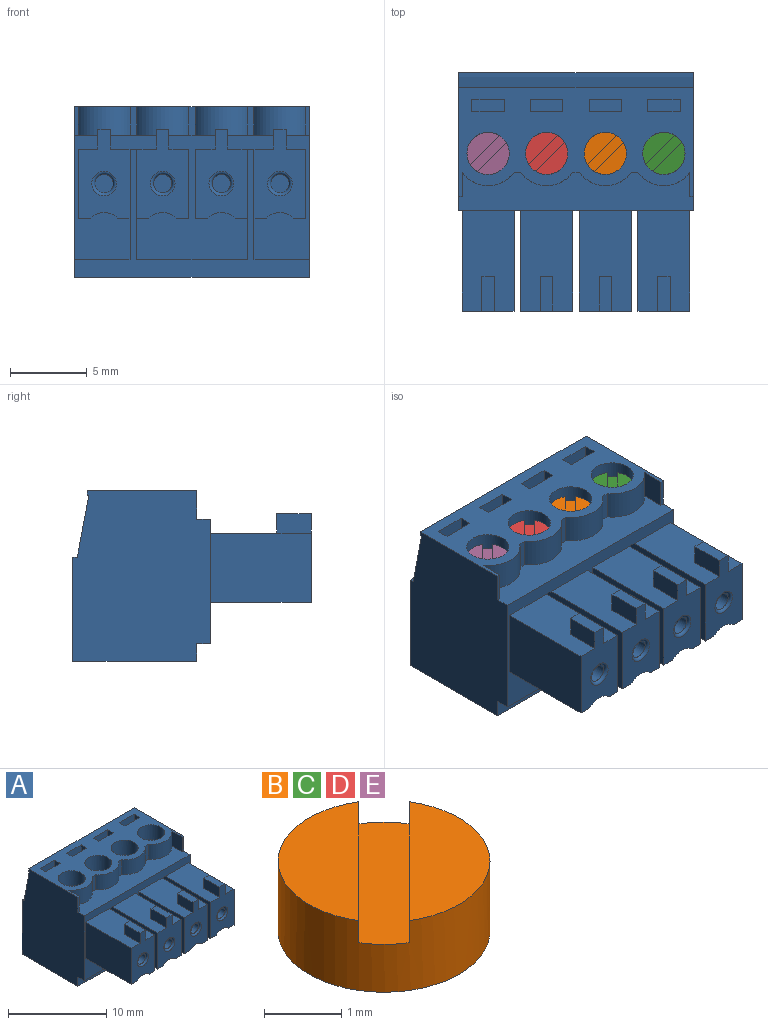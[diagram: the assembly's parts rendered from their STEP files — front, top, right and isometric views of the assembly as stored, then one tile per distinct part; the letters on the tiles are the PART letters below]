
ASSEMBLY  parts=5 mates=1
PART A: 140 faces, bbox 15.2x15.5x11.1 mm
  f0: plane 15.24x7.1mm, normal (0,0,1), area 62.7mm2, adj f5,f11,f12,f28,f29,f31,f39,f59
  f1: plane 15.24x8.34mm, normal (0,-1,0), area 24mm2, adj f3,f4,f5,f6,f16,f52,f58,f75
  f2: plane 15.24x8.08mm, normal (0,-1,0), area 58.1mm2, adj f3,f4,f5,f13,f14,f15,f16,f22
  f3: plane 0.9x0.44mm, normal (0,0,-1), area 0.4mm2, adj f1,f2,f16,f58
  f4: plane 3.59x0.9mm, normal (0,0,-1), area 3.2mm2, adj f1,f2,f5,f16
  f5: plane 11.1x8.95mm, normal (1,0,0), area 93.6mm2, adj f0,f1,f2,f4,f6,f7,f8,f9
  f6: plane 15.24x8.05mm, normal (0,0,-1), area 122.7mm2, adj f1,f5,f7,f77
  f7: plane 15.24x6.78mm, normal (0,1,0), area 55.1mm2, adj f5,f6,f8,f32,f33,f34,f35,f60
  f8: plane 15.24x0.3mm, normal (0,0,1), area 4.5mm2, adj f5,f7,f9,f77
  f9: plane 15.24x4.02mm, normal (0,0.98,0.18), area 62.3mm2, adj f5,f8,f10,f77
  f10: plane 15.24x0.1mm, normal (0,0,-1), area 1.4mm2, adj f5,f9,f11,f77
  f11: plane 15.24x0.3mm, normal (0,1,0), area 4.6mm2, adj f0,f5,f10,f77
  f12: plane 1.86x0.22mm, normal (0,-1,0), area 0.4mm2, adj f0,f5,f13,f28
  f13: plane 15.24x2.46mm, normal (0,0,1), area 28.7mm2, adj f2,f5,f12,f28,f29,f39,f64,f77
  f14: plane 6.55x3.37mm, normal (0,0,1), area 20.3mm2, adj f2,f15,f16,f17,f18,f19,f21
  f15: plane 6.55x4.49mm, normal (1,0,0), area 29.4mm2, adj f2,f14,f17,f22
  f16: plane 7.45x7.18mm, normal (-1,0,0), area 35.9mm2, adj f1,f2,f3,f4,f14,f17,f24
  f17: plane 5.76x3.37mm, normal (0,-1,0), area 13.7mm2, adj f14,f15,f16,f18,f19,f20,f22,f23
  f18: plane 2.25x1.27mm, normal (1,0,0), area 2.9mm2, adj f14,f17,f20,f21
  f19: plane 2.25x1.27mm, normal (-1,0,0), area 2.9mm2, adj f14,f17,f20,f21
  f20: plane 2.25x0.8mm, normal (0,0,1), area 1.8mm2, adj f17,f18,f19,f21
  f21: plane 1.27x0.8mm, normal (0,1,0), area 1mm2, adj f14,f18,f19,f20
  f22: plane 6.55x0.79mm, normal (0,0,-1), area 5.1mm2, adj f2,f15,f17,f23
  f23: cylinder r=1.3mm len=6.55mm, axis (0,1,0), area 13mm2, adj f2,f17,f22,f24
  f24: plane 6.55x0.79mm, normal (0,0,-1), area 5.1mm2, adj f2,f16,f17,f23
  f25: plane 1.2x1.2mm, normal (0,-1,0), area 1.1mm2, adj f26
  f26: cylinder r=0.6mm len=6.35mm, axis (0,1,0), area 24mm2, adj f25,f27
  f27: torus R=0.8mm, axis (0,-1,0), area 1.3mm2, adj f17,f26
  f28: plane 1.86x1.56mm, normal (-1,0,0), area 2.9mm2, adj f0,f12,f13,f29
  f29: cylinder r=2.1mm len=3.37mm, axis (0,0,-1), area 7.3mm2, adj f0,f13,f28,f39
  f30: plane 2.75x2.75mm, normal (0,0,1), area 5.9mm2, adj f31
  f31: cylinder r=1.38mm len=2.75mm, axis (0,0,-1), area 16.1mm2, adj f0,f30
  f32: plane 3.58x2mm, normal (-0.98,0.21,0), area 6.5mm2, adj f7,f33,f35,f36
  f33: plane 3.37x2mm, normal (0,0.21,-0.98), area 6mm2, adj f7,f32,f34,f36
  f34: plane 3.58x2mm, normal (0.98,0.21,0), area 6.5mm2, adj f7,f33,f35,f36
  f35: plane 3.37x2mm, normal (0,0.21,0.98), area 6mm2, adj f7,f32,f34,f36
  f36: plane 2.73x2.52mm, normal (0,1,0), area 4.8mm2, adj f32,f33,f34,f35,f38
  f37: plane 1.63x1.63mm, normal (0,1,0), area 2.1mm2, adj f38
  f38: cylinder r=0.81mm len=4.8mm, axis (0,-1,0), area 24.6mm2, adj f36,f37
  f39: plane 1.86x0.44mm, normal (0,-1,0), area 0.8mm2, adj f0,f13,f29,f64
  f40: plane 1.2x1.2mm, normal (0,-1,0), area 1.1mm2, adj f41
  f41: cylinder r=0.6mm len=6.35mm, axis (0,1,0), area 24mm2, adj f40,f44
  f42: plane 1.63x1.63mm, normal (0,1,0), area 2.1mm2, adj f45
  f43: plane 2.25x0.8mm, normal (0,0,1), area 1.8mm2, adj f46,f47,f48,f49
  f44: torus R=0.8mm, axis (0,-1,0), area 1.3mm2, adj f41,f49
  f45: cylinder r=0.81mm len=4.8mm, axis (0,-1,0), area 24.6mm2, adj f42,f51
  f46: plane 2.25x1.27mm, normal (1,0,0), area 2.9mm2, adj f43,f48,f49,f57
  f47: plane 2.25x1.27mm, normal (-1,0,0), area 2.9mm2, adj f43,f48,f49,f57
  f48: plane 1.27x0.8mm, normal (0,1,0), area 1mm2, adj f43,f46,f47,f57
  f49: plane 5.76x3.37mm, normal (0,-1,0), area 13.7mm2, adj f43,f44,f46,f47,f53,f54,f55,f56
  f50: plane 2.75x2.75mm, normal (0,0,1), area 5.9mm2, adj f59
  f51: plane 2.73x2.52mm, normal (0,1,0), area 4.8mm2, adj f45,f60,f61,f62,f63
  f52: plane 7.18x0.9mm, normal (0,0,-1), area 6.5mm2, adj f1,f2,f58,f122
  f53: plane 6.55x0.79mm, normal (0,0,-1), area 5.1mm2, adj f2,f49,f54,f58
  f54: cylinder r=1.3mm len=6.55mm, axis (0,1,0), area 13mm2, adj f2,f49,f53,f55
  f55: plane 6.55x0.79mm, normal (0,0,-1), area 5.1mm2, adj f2,f49,f54,f56
  f56: plane 6.55x4.49mm, normal (-1,0,0), area 29.4mm2, adj f2,f49,f55,f57
  f57: plane 6.55x3.37mm, normal (0,0,1), area 20.3mm2, adj f2,f46,f47,f48,f49,f56,f58
  f58: plane 7.45x7.18mm, normal (1,0,0), area 35.9mm2, adj f1,f2,f3,f49,f52,f53,f57
  f59: cylinder r=1.38mm len=2.75mm, axis (0,0,-1), area 16.1mm2, adj f0,f50
  f60: plane 3.58x2mm, normal (-0.98,0.21,0), area 6.5mm2, adj f7,f51,f61,f63
  f61: plane 3.37x2mm, normal (0,0.21,-0.98), area 6mm2, adj f7,f51,f60,f62
  f62: plane 3.58x2mm, normal (0.98,0.21,0), area 6.5mm2, adj f7,f51,f61,f63
  f63: plane 3.37x2mm, normal (0,0.21,0.98), area 6mm2, adj f7,f51,f60,f62
  f64: cylinder r=2.1mm len=3.37mm, axis (0,0,-1), area 7.3mm2, adj f0,f13,f39,f139
  f65: plane 2.1x1.86mm, normal (0,-1,0), area 3.9mm2, adj f0,f66,f68,f69
  f66: plane 1.86x0.8mm, normal (1,0,0), area 1.5mm2, adj f0,f65,f67,f69
  f67: plane 2.1x1.86mm, normal (0,1,0), area 3.9mm2, adj f0,f66,f68,f69
  f68: plane 1.86x0.8mm, normal (-1,0,0), area 1.5mm2, adj f0,f65,f67,f69
  f69: plane 2.1x0.8mm, normal (0,0,1), area 1.7mm2, adj f65,f66,f67,f68
  f70: plane 2.1x1.86mm, normal (0,1,0), area 3.9mm2, adj f0,f71,f73,f74
  f71: plane 1.86x0.8mm, normal (-1,0,0), area 1.5mm2, adj f0,f70,f72,f74
  f72: plane 2.1x1.86mm, normal (0,-1,0), area 3.9mm2, adj f0,f71,f73,f74
  f73: plane 1.86x0.8mm, normal (1,0,0), area 1.5mm2, adj f0,f70,f72,f74
  f74: plane 2.1x0.8mm, normal (0,0,1), area 1.7mm2, adj f70,f71,f72,f73
  f75: plane 0.9x0.44mm, normal (0,0,-1), area 0.4mm2, adj f1,f2,f81,f122
  f76: plane 3.59x0.9mm, normal (0,0,-1), area 3.2mm2, adj f1,f2,f77,f81
  f77: plane 11.1x8.95mm, normal (-1,0,0), area 93.6mm2, adj f0,f1,f2,f6,f7,f8,f9,f10
  f78: plane 1.86x0.22mm, normal (0,-1,0), area 0.4mm2, adj f0,f13,f77,f93
  f79: plane 6.55x3.37mm, normal (0,0,1), area 20.3mm2, adj f2,f80,f81,f82,f83,f84,f86
  f80: plane 6.55x4.49mm, normal (-1,0,0), area 29.4mm2, adj f2,f79,f82,f87
  f81: plane 7.45x7.18mm, normal (1,0,0), area 35.9mm2, adj f1,f2,f75,f76,f79,f82,f89
  f82: plane 5.76x3.37mm, normal (0,-1,0), area 13.7mm2, adj f79,f80,f81,f83,f84,f85,f87,f88
  f83: plane 2.25x1.27mm, normal (-1,0,0), area 2.9mm2, adj f79,f82,f85,f86
  f84: plane 2.25x1.27mm, normal (1,0,0), area 2.9mm2, adj f79,f82,f85,f86
  f85: plane 2.25x0.8mm, normal (0,0,1), area 1.8mm2, adj f82,f83,f84,f86
  f86: plane 1.27x0.8mm, normal (0,1,0), area 1mm2, adj f79,f83,f84,f85
  f87: plane 6.55x0.79mm, normal (0,0,-1), area 5.1mm2, adj f2,f80,f82,f88
  f88: cylinder r=1.3mm len=6.55mm, axis (0,1,0), area 13mm2, adj f2,f82,f87,f89
  f89: plane 6.55x0.79mm, normal (0,0,-1), area 5.1mm2, adj f2,f81,f82,f88
  f90: plane 1.2x1.2mm, normal (0,-1,0), area 1.1mm2, adj f91
  f91: cylinder r=0.6mm len=6.35mm, axis (0,1,0), area 24mm2, adj f90,f92
  f92: torus R=0.8mm, axis (0,-1,0), area 1.3mm2, adj f82,f91
  f93: plane 1.86x1.56mm, normal (1,0,0), area 2.9mm2, adj f0,f13,f78,f94
  f94: cylinder r=2.1mm len=3.37mm, axis (0,0,-1), area 7.3mm2, adj f0,f13,f93,f104
  f95: plane 2.75x2.75mm, normal (0,0,1), area 5.9mm2, adj f96
  f96: cylinder r=1.38mm len=2.75mm, axis (0,0,-1), area 16.1mm2, adj f0,f95
  f97: plane 3.58x2mm, normal (0.98,0.21,0), area 6.5mm2, adj f7,f98,f100,f101
  f98: plane 3.37x2mm, normal (0,0.21,-0.98), area 6mm2, adj f7,f97,f99,f101
  f99: plane 3.58x2mm, normal (-0.98,0.21,0), area 6.5mm2, adj f7,f98,f100,f101
  f100: plane 3.37x2mm, normal (0,0.21,0.98), area 6mm2, adj f7,f97,f99,f101
  f101: plane 2.73x2.52mm, normal (0,1,0), area 4.8mm2, adj f97,f98,f99,f100,f103
  f102: plane 1.63x1.63mm, normal (0,1,0), area 2.1mm2, adj f103
  f103: cylinder r=0.81mm len=4.8mm, axis (0,-1,0), area 24.6mm2, adj f101,f102
  f104: plane 1.86x0.44mm, normal (0,-1,0), area 0.8mm2, adj f0,f13,f94,f128
  f105: plane 1.2x1.2mm, normal (0,-1,0), area 1.1mm2, adj f106
  f106: cylinder r=0.6mm len=6.35mm, axis (0,1,0), area 24mm2, adj f105,f109
  f107: plane 1.63x1.63mm, normal (0,1,0), area 2.1mm2, adj f110
  f108: plane 2.25x0.8mm, normal (0,0,1), area 1.8mm2, adj f111,f112,f113,f114
  f109: torus R=0.8mm, axis (0,-1,0), area 1.3mm2, adj f106,f114
  f110: cylinder r=0.81mm len=4.8mm, axis (0,-1,0), area 24.6mm2, adj f107,f116
  f111: plane 2.25x1.27mm, normal (-1,0,0), area 2.9mm2, adj f108,f113,f114,f121
  f112: plane 2.25x1.27mm, normal (1,0,0), area 2.9mm2, adj f108,f113,f114,f121
  f113: plane 1.27x0.8mm, normal (0,1,0), area 1mm2, adj f108,f111,f112,f121
  f114: plane 5.76x3.37mm, normal (0,-1,0), area 13.7mm2, adj f108,f109,f111,f112,f117,f118,f119,f120
  f115: plane 2.75x2.75mm, normal (0,0,1), area 5.9mm2, adj f123
  f116: plane 2.73x2.52mm, normal (0,1,0), area 4.8mm2, adj f110,f124,f125,f126,f127
  f117: plane 6.55x0.79mm, normal (0,0,-1), area 5.1mm2, adj f2,f114,f118,f122
  f118: cylinder r=1.3mm len=6.55mm, axis (0,1,0), area 13mm2, adj f2,f114,f117,f119
  f119: plane 6.55x0.79mm, normal (0,0,-1), area 5.1mm2, adj f2,f114,f118,f120
  f120: plane 6.55x4.49mm, normal (1,0,0), area 29.4mm2, adj f2,f114,f119,f121
  f121: plane 6.55x3.37mm, normal (0,0,1), area 20.3mm2, adj f2,f111,f112,f113,f114,f120,f122
  f122: plane 7.45x7.18mm, normal (-1,0,0), area 35.9mm2, adj f1,f2,f52,f75,f114,f117,f121
  f123: cylinder r=1.38mm len=2.75mm, axis (0,0,-1), area 16.1mm2, adj f0,f115
  f124: plane 3.58x2mm, normal (0.98,0.21,0), area 6.5mm2, adj f7,f116,f125,f127
  f125: plane 3.37x2mm, normal (0,0.21,-0.98), area 6mm2, adj f7,f116,f124,f126
  f126: plane 3.58x2mm, normal (-0.98,0.21,0), area 6.5mm2, adj f7,f116,f125,f127
  f127: plane 3.37x2mm, normal (0,0.21,0.98), area 6mm2, adj f7,f116,f124,f126
  f128: cylinder r=2.1mm len=3.37mm, axis (0,0,-1), area 7.3mm2, adj f0,f13,f104,f139
  f129: plane 2.1x1.86mm, normal (0,-1,0), area 3.9mm2, adj f0,f130,f132,f133
  f130: plane 1.86x0.8mm, normal (-1,0,0), area 1.5mm2, adj f0,f129,f131,f133
  f131: plane 2.1x1.86mm, normal (0,1,0), area 3.9mm2, adj f0,f130,f132,f133
  f132: plane 1.86x0.8mm, normal (1,0,0), area 1.5mm2, adj f0,f129,f131,f133
  f133: plane 2.1x0.8mm, normal (0,0,1), area 1.7mm2, adj f129,f130,f131,f132
  f134: plane 2.1x1.86mm, normal (0,1,0), area 3.9mm2, adj f0,f135,f137,f138
  f135: plane 1.86x0.8mm, normal (1,0,0), area 1.5mm2, adj f0,f134,f136,f138
  f136: plane 2.1x1.86mm, normal (0,-1,0), area 3.9mm2, adj f0,f135,f137,f138
  f137: plane 1.86x0.8mm, normal (-1,0,0), area 1.5mm2, adj f0,f134,f136,f138
  f138: plane 2.1x0.8mm, normal (0,0,1), area 1.7mm2, adj f134,f135,f136,f137
  f139: plane 1.86x0.44mm, normal (0,-1,0), area 0.8mm2, adj f0,f13,f64,f128
PART B: 7 faces, bbox 2.8x2.8x1.1 mm
  f0: plane 2.09x2.09mm, normal (0,0,1), area 2.1mm2, adj f1,f5
  f1: cylinder r=1.38mm len=2.75mm, axis (0,0,-1), area 9.1mm2, adj f0,f2,f3,f4,f5,f6
  f2: plane 2.09x2.09mm, normal (0,0,1), area 2.1mm2, adj f1,f4
  f3: plane 2.75x2.75mm, normal (0,0,-1), area 5.9mm2, adj f1
  f4: plane 1.89x1.89mm, normal (0.71,-0.71,0), area 0.9mm2, adj f1,f2,f6
  f5: plane 1.89x1.89mm, normal (-0.71,0.71,0), area 0.9mm2, adj f0,f1,f6
  f6: plane 2.35x2.35mm, normal (0,0,1), area 1.8mm2, adj f1,f4,f5
PART C: same geometry as B
PART D: same geometry as B
PART E: same geometry as B
PLACE A t=(-1.03,-2.76,0.74)mm
PLACE B t=(-1.03,-2.76,0.74)mm
PLACE C t=(2.78,-2.76,0.74)mm
PLACE D t=(-4.84,-2.76,0.74)mm
PLACE E t=(-8.65,-2.76,0.74)mm
MATE fastened E.f1 <-> A.f94  axis (0,0,-1) through (-8.66,0.94,4.43)mm
